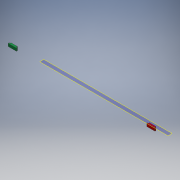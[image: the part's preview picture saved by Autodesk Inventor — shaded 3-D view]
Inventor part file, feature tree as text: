
AUTODESK INVENTOR PART (.ipt)
format: ipt  version: 2018 (Build 220112000, 112)  size: 152,064 bytes
history: native  units: in
note: dims shown in document units (in); Inventor stores cm internally (conversion verified against a paired STEP export)
features: reference x14, sketch x4, extrude x4, plane x3, other x3, fillet x2, projected_geometry x2
ambient origin geometry x8: Origin, YZ Plane, XZ Plane, XY Plane, X Axis, Y Axis, Z Axis, Center Point
bodies: Solid1 (feature_tree), Solid2 (feature_tree)
feature tree (32):
  plane  "Work Plane1"
  sketch  "Sketch2"  dims[d0=1.0in d1=0.0in d2=0.005in d3=0.0in]
  plane  "Work Plane2"
  extrude  "Extrusion1"  Depth=0.005in TaperAngle=0.0deg
  extrude  "Extrusion2"  Depth=0.005in TaperAngle=0.0deg
  sketch  "Sketch5"  dims[d8=0.005in d9=0.005in]
  plane  "Work Plane3"
  extrude  "Extrusion3"  Depth=0.005in
  extrude  "Extrusion4"  [1 undecoded]
  fillet  "Fillet1"  [1 undecoded]
  fillet  "Fillet2"  [1 undecoded]
  reference  "Reference1"
  reference  "Reference2"
  reference  "Reference3"
  reference  "Reference4"
  reference  "Reference5"
  reference  "Reference6"
  reference  "Reference7"
  sketch  "Sketch3"  dims[d4=0.005in d5=0.0in d6=0.005in d7=0.0in]
  projected_geometry  "Projected Loop1"
  reference  "Reference8"
  reference  "Reference9"
  reference  "Reference10"
  reference  "Reference11"
  reference  "Reference12"
  reference  "Reference13"
  reference  "Reference14"
  sketch  "Sketch6"
  projected_geometry  "Projected Loop2"
  other  "<userpath>\Documents\Commodore Cube Project\Case\Assembly.iam"
  other  "Assembly.iam"
  other  "Tray:1"
note: 3 required parameter values undecoded (feature->parameter linkage not recoverable at this tier; creation-order binding heuristic only, values carry confidence <= 0.55)
